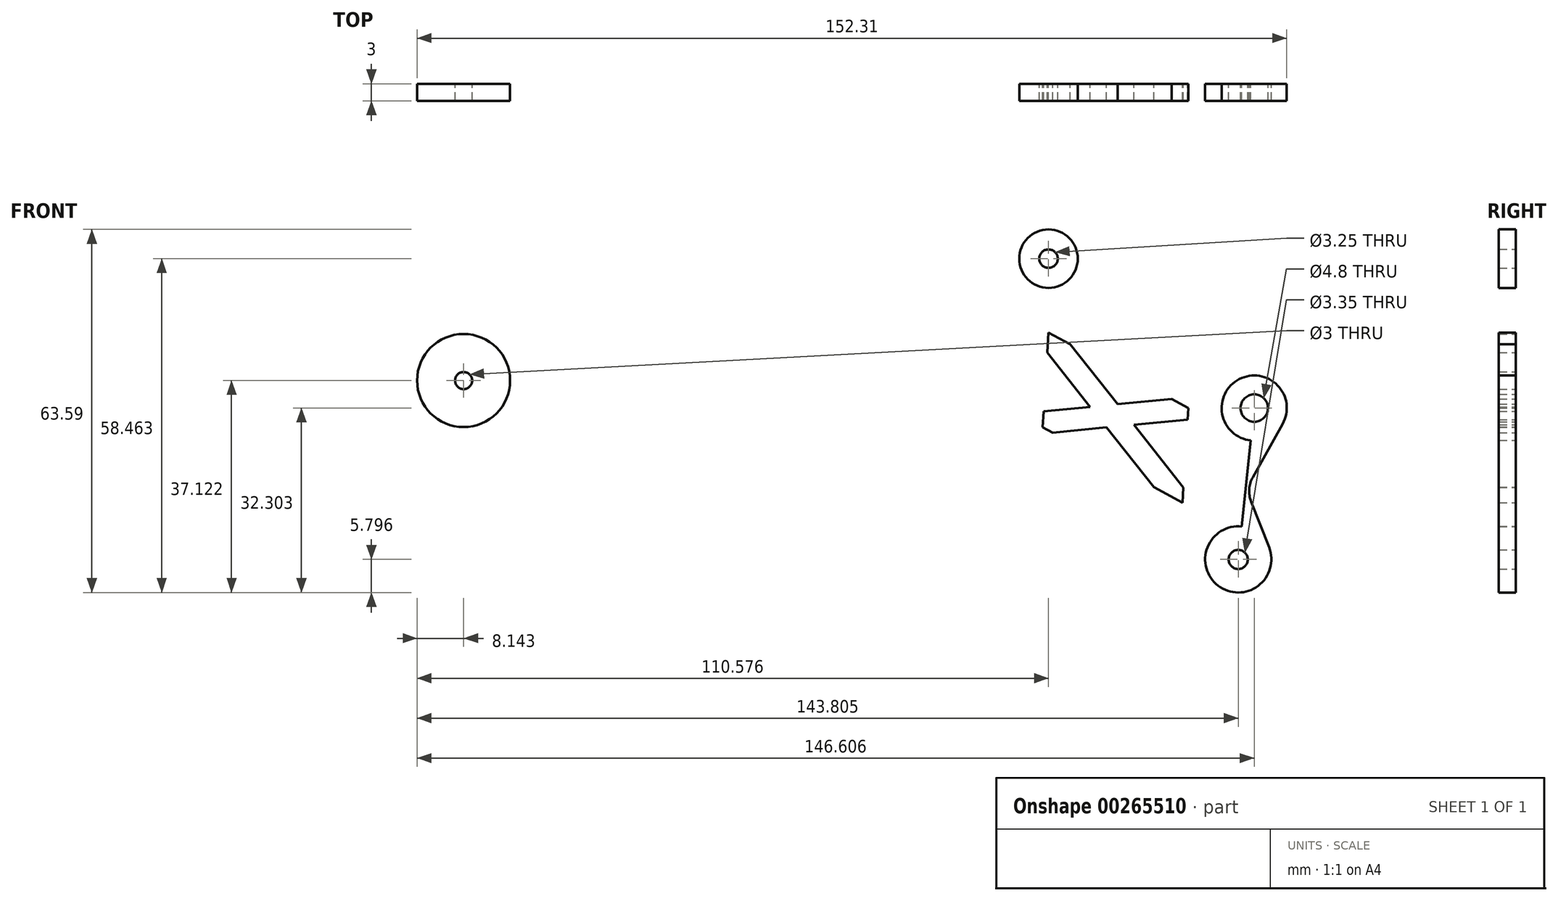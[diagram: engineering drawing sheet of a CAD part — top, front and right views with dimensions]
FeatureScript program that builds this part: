
annotation { "Feature Type Name" : "Feature", "Feature Type Description" : "" }
export const myFeature = defineFeature(function(context is Context, id is Id, definition is map)
    precondition{}
    {
        {
            var Q0;
            Q0=qCreatedBy(makeId("Front.planeOp"),FACE);
            var sketch = newSketch(context, id + "F0", { "sketchPlane" : qUnion([Q0])});
            skLineSegment(sketch, "E0", {"start": v(-62, 21.3) * mm, "end": v(-26.39, 21.3) * mm, "construction": true});
            skLineSegment(sketch, "E1", {"start": v(-44.19, 33.22) * mm, "end": v(-44.19, 9.36) * mm, "construction": true});
            skCircle(sketch, "E2", {"center": v(-44.19, 21.3) * mm, "radius": 8 * mm});
            skLineSegment(sketch, "E3", {"start": v(-44.19, 21.3) * mm, "end": v(-44.19, 31.84) * mm, "construction": true});
            skCircle(sketch, "E4", {"center": v(-44.19, 31.84) * mm, "radius": 1.35 * mm});
            skLineSegment(sketch, "E5.MirrorCS", {"start": v(-44.19, 21.3) * mm, "end": v(-44.19, 10.74) * mm, "construction": true});
            skCircle(sketch, "E6.MirrorC", {"center": v(-44.19, 10.74) * mm, "radius": 1.35 * mm});
            skCircle(sketch, "E7", {"center": v(-14.5, 21.05) * mm, "radius": 18.1 * mm});
            skLineSegment(sketch, "E8", {"start": v(-14.5, 21.05) * mm, "end": v(-8.7, 21.05) * mm, "construction": true});
            skCircle(sketch, "E9", {"center": v(-8.7, 21.05) * mm, "radius": 18.1 * mm});
            skLineSegment(sketch, "E10", {"start": v(-46.93, 21.05) * mm, "end": v(14.5, 21.05) * mm, "construction": true});
            skLineSegment(sketch, "E11", {"start": v(-27, 0) * mm, "end": v(27, 0) * mm});
            skLineSegment(sketch, "E12", {"start": v(-14.5, 2.95) * mm, "end": v(-8.7, 2.95) * mm});
            skLineSegment(sketch, "E13", {"start": v(27, 0) * mm, "end": v(27, 96) * mm, "construction": true});
            skLineSegment(sketch, "E14", {"start": v(-27, 0) * mm, "end": v(-27, 100) * mm, "construction": true});
            skLineSegment(sketch, "E15", {"start": v(-27, 100) * mm, "end": v(27, 96) * mm});
            skLineSegment(sketch, "E16", {"start": v(27, 96) * mm, "end": v(32.9, 95.56) * mm});
            skLineSegment(sketch, "E17", {"start": v(-56.51, 95.62) * mm, "end": v(-9.94, 92.16) * mm, "construction": true});
            skLineSegment(sketch, "E18.bottom", {"start": v(-7.95, 92) * mm, "end": v(29.75, 89.22) * mm});
            skLineSegment(sketch, "E18.top", {"start": v(-9.55, 70.37) * mm, "end": v(28.15, 67.58) * mm});
            skLineSegment(sketch, "E18.left", {"start": v(-10.09, 90.16) * mm, "end": v(-11.4, 72.5) * mm});
            skLineSegment(sketch, "E18.right", {"start": v(31.6, 87.07) * mm, "end": v(30.29, 69.42) * mm});
            skLineSegment(sketch, "E19", {"start": v(-10.74, 81.34) * mm, "end": v(-13.74, 81.56) * mm, "construction": true});
            skLineSegment(sketch, "E20", {"start": v(-10.74, 81.34) * mm, "end": v(-10.52, 84.33) * mm, "construction": true});
            skArc(sketch, "E21", {"start": v(-13.74, 81.56) * mm, "mid": v(-12.7, 83.6) * mm, "end": v(-10.52, 84.33) * mm});
            skArc(sketch, "E22", {"start": v(-13.74, 81.56) * mm, "mid": v(-13.02, 79.38) * mm, "end": v(-10.97, 78.34) * mm});
            skLineSegment(sketch, "E23", {"start": v(10.9, 90.61) * mm, "end": v(9.3, 68.97) * mm, "construction": true});
            skArc(sketch, "E24.MirrorCS", {"start": v(33.93, 78.03) * mm, "mid": v(32.9, 75.98) * mm, "end": v(30.72, 75.26) * mm});
            skArc(sketch, "E25.MirrorCS", {"start": v(33.93, 78.03) * mm, "mid": v(33.21, 80.2) * mm, "end": v(31.16, 81.24) * mm});
            skLineSegment(sketch, "E26", {"start": v(-10.74, 81.34) * mm, "end": v(-10.36, 86.47) * mm, "construction": true});
            skLineSegment(sketch, "E27", {"start": v(-10.36, 86.47) * mm, "end": v(-13.9, 86.73) * mm, "construction": true});
            skCircle(sketch, "E28", {"center": v(-13.9, 86.73) * mm, "radius": 1.55 * mm});
            skCircle(sketch, "E29.MirrorC", {"center": v(-14.66, 76.46) * mm, "radius": 1.55 * mm});
            skLineSegment(sketch, "E30.MirrorCS", {"start": v(-11.12, 76.2) * mm, "end": v(-14.66, 76.46) * mm, "construction": true});
            skLineSegment(sketch, "E31.MirrorCS", {"start": v(-10.74, 81.34) * mm, "end": v(-11.12, 76.2) * mm, "construction": true});
            skLineSegment(sketch, "E32.MirrorCS", {"start": v(30.56, 73.11) * mm, "end": v(34.1, 72.85) * mm, "construction": true});
            skCircle(sketch, "E33.MirrorC", {"center": v(34.1, 72.85) * mm, "radius": 1.55 * mm});
            skCircle(sketch, "E34.MirrorC", {"center": v(34.86, 83.12) * mm, "radius": 1.55 * mm});
            skLineSegment(sketch, "E35.MirrorCS", {"start": v(31.32, 83.38) * mm, "end": v(34.86, 83.12) * mm, "construction": true});
            skPoint(sketch, "E36.visualSharp", {"position": v(-9.94, 92.16) * mm});
            skArc(sketch, "E36.filletArc", {"start": v(-7.95, 92) * mm, "mid": v(-9.4, 91.53) * mm, "end": v(-10.09, 90.16) * mm});
            skPoint(sketch, "E37.visualSharp", {"position": v(-11.54, 70.52) * mm});
            skArc(sketch, "E37.filletArc", {"start": v(-11.4, 72.5) * mm, "mid": v(-10.92, 71.06) * mm, "end": v(-9.55, 70.37) * mm});
            skPoint(sketch, "E38.visualSharp", {"position": v(31.74, 89.07) * mm});
            skArc(sketch, "E38.filletArc", {"start": v(31.6, 87.07) * mm, "mid": v(31.12, 88.53) * mm, "end": v(29.75, 89.22) * mm});
            skPoint(sketch, "E39.visualSharp", {"position": v(30.14, 67.43) * mm});
            skArc(sketch, "E39.filletArc", {"start": v(28.15, 67.58) * mm, "mid": v(29.6, 68.06) * mm, "end": v(30.29, 69.42) * mm});
            skLineSegment(sketch, "E40.bottom", {"start": v(17.59, 51.31) * mm, "end": v(55.28, 48.52) * mm});
            skLineSegment(sketch, "E40.top", {"start": v(15.98, 29.67) * mm, "end": v(53.68, 26.88) * mm});
            skLineSegment(sketch, "E40.left", {"start": v(15.44, 49.46) * mm, "end": v(14.14, 31.81) * mm});
            skLineSegment(sketch, "E40.right", {"start": v(57.13, 46.38) * mm, "end": v(55.82, 28.72) * mm});
            skLineSegment(sketch, "E41", {"start": v(14.79, 40.64) * mm, "end": v(11.8, 40.86) * mm, "construction": true});
            skLineSegment(sketch, "E42", {"start": v(14.79, 40.64) * mm, "end": v(15.01, 43.63) * mm, "construction": true});
            skArc(sketch, "E43", {"start": v(11.8, 40.86) * mm, "mid": v(12.83, 42.91) * mm, "end": v(15.01, 43.63) * mm});
            skArc(sketch, "E44", {"start": v(11.8, 40.86) * mm, "mid": v(12.52, 38.68) * mm, "end": v(14.57, 37.65) * mm});
            skLineSegment(sketch, "E45", {"start": v(36.43, 49.91) * mm, "end": v(34.83, 28.27) * mm, "construction": true});
            skArc(sketch, "E46.MirrorCS", {"start": v(59.47, 37.33) * mm, "mid": v(58.43, 35.28) * mm, "end": v(56.25, 34.56) * mm});
            skArc(sketch, "E47.MirrorCS", {"start": v(59.47, 37.33) * mm, "mid": v(58.75, 39.5) * mm, "end": v(56.7, 40.54) * mm});
            skLineSegment(sketch, "E48", {"start": v(14.79, 40.64) * mm, "end": v(15.17, 45.77) * mm, "construction": true});
            skLineSegment(sketch, "E49", {"start": v(15.17, 45.77) * mm, "end": v(11.63, 46.04) * mm, "construction": true});
            skCircle(sketch, "E50", {"center": v(11.63, 46.04) * mm, "radius": 1.55 * mm});
            skCircle(sketch, "E51.MirrorC", {"center": v(10.87, 35.76) * mm, "radius": 1.55 * mm});
            skLineSegment(sketch, "E52.MirrorCS", {"start": v(14.4, 35.5) * mm, "end": v(10.87, 35.76) * mm, "construction": true});
            skLineSegment(sketch, "E53.MirrorCS", {"start": v(14.79, 40.64) * mm, "end": v(14.4, 35.5) * mm, "construction": true});
            skLineSegment(sketch, "E54.MirrorCS", {"start": v(56.1, 32.41) * mm, "end": v(59.64, 32.15) * mm, "construction": true});
            skCircle(sketch, "E55.MirrorC", {"center": v(59.64, 32.15) * mm, "radius": 1.55 * mm});
            skCircle(sketch, "E56.MirrorC", {"center": v(60.4, 42.42) * mm, "radius": 1.55 * mm});
            skLineSegment(sketch, "E57.MirrorCS", {"start": v(56.86, 42.69) * mm, "end": v(60.4, 42.42) * mm, "construction": true});
            skPoint(sketch, "E58.visualSharp", {"position": v(15.6, 51.46) * mm});
            skArc(sketch, "E58.filletArc", {"start": v(17.59, 51.31) * mm, "mid": v(16.13, 50.83) * mm, "end": v(15.44, 49.46) * mm});
            skPoint(sketch, "E59.visualSharp", {"position": v(13.99, 29.82) * mm});
            skArc(sketch, "E59.filletArc", {"start": v(14.14, 31.81) * mm, "mid": v(14.62, 30.36) * mm, "end": v(15.98, 29.67) * mm});
            skPoint(sketch, "E60.visualSharp", {"position": v(57.28, 48.37) * mm});
            skArc(sketch, "E60.filletArc", {"start": v(57.13, 46.38) * mm, "mid": v(56.65, 47.83) * mm, "end": v(55.28, 48.52) * mm});
            skPoint(sketch, "E61.visualSharp", {"position": v(55.67, 26.73) * mm});
            skArc(sketch, "E61.filletArc", {"start": v(53.68, 26.88) * mm, "mid": v(55.13, 27.36) * mm, "end": v(55.82, 28.72) * mm});
            skLineSegment(sketch, "E62", {"start": v(30.14, 67.43) * mm, "end": v(28.89, 50.47) * mm, "construction": true});
            skLineSegment(sketch, "E63", {"start": v(28.89, 50.47) * mm, "end": v(15.6, 51.46) * mm, "construction": true});
            skLineSegment(sketch, "E64", {"start": v(55.67, 26.73) * mm, "end": v(53.66, -0.52) * mm, "construction": true});
            skLineSegment(sketch, "E65", {"start": v(53.66, -0.52) * mm, "end": v(46.68, 0) * mm, "construction": true});
            skLineSegment(sketch, "E66", {"start": v(27, 0) * mm, "end": v(46.68, 0) * mm});
            skLineSegment(sketch, "E67", {"start": v(60.4, 42.42) * mm, "end": v(88.4, 62) * mm, "construction": true});
            skLineSegment(sketch, "E68", {"start": v(34.1, 72.85) * mm, "end": v(88.4, 62) * mm, "construction": true});
            skCircle(sketch, "E69", {"center": v(88.4, 62) * mm, "radius": 1.68 * mm});
            skLineSegment(sketch, "E70", {"start": v(60.4, 42.42) * mm, "end": v(69.22, 57.07) * mm, "construction": true});
            skLineSegment(sketch, "E71", {"start": v(34.1, 72.85) * mm, "end": v(69.22, 57.07) * mm, "construction": true});
            skCircle(sketch, "E72", {"center": v(69.22, 57.07) * mm, "radius": 2 * mm});
            skLineSegment(sketch, "E73", {"start": v(60.4, 42.42) * mm, "end": v(77.84, 65.53) * mm, "construction": true});
            skLineSegment(sketch, "E74", {"start": v(34.1, 72.85) * mm, "end": v(77.84, 65.53) * mm, "construction": true});
            skCircle(sketch, "E75", {"center": v(77.84, 65.53) * mm, "radius": 1.25 * mm});
            skLineSegment(sketch, "E76", {"start": v(59.64, 32.15) * mm, "end": v(91.2, 88.51) * mm, "construction": true});
            skLineSegment(sketch, "E77", {"start": v(34.86, 83.12) * mm, "end": v(91.2, 88.51) * mm, "construction": true});
            skCircle(sketch, "E78", {"center": v(91.2, 88.51) * mm, "radius": 2.4 * mm});
            skLineSegment(sketch, "E79", {"start": v(59.64, 32.15) * mm, "end": v(34.5, 58.07) * mm, "construction": true});
            skLineSegment(sketch, "E80", {"start": v(10.87, 35.76) * mm, "end": v(34.5, 58.07) * mm, "construction": true});
            skCircle(sketch, "E81", {"center": v(34.5, 58.07) * mm, "radius": 2 * mm});
            skLineSegment(sketch, "E82", {"start": v(34.86, 83.12) * mm, "end": v(55.18, 114.67) * mm, "construction": true});
            skLineSegment(sketch, "E83", {"start": v(91.2, 88.51) * mm, "end": v(55.18, 114.67) * mm, "construction": true});
            skCircle(sketch, "E84", {"center": v(55.18, 114.67) * mm, "radius": 1.63 * mm});
            skLineSegment(sketch, "E85", {"start": v(59.64, 32.15) * mm, "end": v(13.17, 19.73) * mm, "construction": true});
            skLineSegment(sketch, "E86", {"start": v(10.87, 35.76) * mm, "end": v(13.17, 19.73) * mm, "construction": true});
            skCircle(sketch, "E87", {"center": v(13.17, 19.73) * mm, "radius": 1.5 * mm});
            skLineSegment(sketch, "E88", {"start": v(59.64, 32.15) * mm, "end": v(15.67, 5.14) * mm, "construction": true});
            skLineSegment(sketch, "E89", {"start": v(15.67, 5.14) * mm, "end": v(10.87, 35.76) * mm, "construction": true});
            skCircle(sketch, "E90", {"center": v(15.67, 5.14) * mm, "radius": 1.5 * mm});
            skLineSegment(sketch, "E91", {"start": v(59.64, 32.15) * mm, "end": v(4.5, 5.12) * mm, "construction": true});
            skLineSegment(sketch, "E92", {"start": v(4.5, 5.12) * mm, "end": v(10.87, 35.76) * mm, "construction": true});
            skCircle(sketch, "E93", {"center": v(4.5, 5.12) * mm, "radius": 1.5 * mm});
            skLineSegment(sketch, "E94", {"start": v(-14.66, 76.46) * mm, "end": v(5.35, 55.37) * mm, "construction": true});
            skLineSegment(sketch, "E95", {"start": v(11.63, 46.04) * mm, "end": v(5.35, 55.37) * mm, "construction": true});
            skLineSegment(sketch, "E96", {"start": v(11.63, 46.04) * mm, "end": v(-9.77, 54.86) * mm, "construction": true});
            skLineSegment(sketch, "E97", {"start": v(-9.77, 54.86) * mm, "end": v(-14.66, 76.46) * mm, "construction": true});
            skLineSegment(sketch, "E98", {"start": v(11.63, 46.04) * mm, "end": v(-18.73, 56.32) * mm, "construction": true});
            skLineSegment(sketch, "E99", {"start": v(-18.73, 56.32) * mm, "end": v(-14.66, 76.46) * mm, "construction": true});
            skCircle(sketch, "E100", {"center": v(5.35, 55.37) * mm, "radius": 1.5 * mm});
            skCircle(sketch, "E101", {"center": v(-9.77, 54.86) * mm, "radius": 1.6 * mm});
            skCircle(sketch, "E102", {"center": v(-18.73, 56.32) * mm, "radius": 1.6 * mm});
            skLineSegment(sketch, "E103", {"start": v(11.63, 46.04) * mm, "end": v(-22.31, 42.26) * mm, "construction": true});
            skLineSegment(sketch, "E104", {"start": v(-22.31, 42.26) * mm, "end": v(-14.66, 76.46) * mm, "construction": true});
            skCircle(sketch, "E105", {"center": v(-22.31, 42.26) * mm, "radius": 1.5 * mm});
            skLineSegment(sketch, "E106", {"start": v(11.63, 46.04) * mm, "end": v(-34.4, 4.89) * mm, "construction": true});
            skLineSegment(sketch, "E107", {"start": v(-34.4, 4.89) * mm, "end": v(-14.66, 76.46) * mm, "construction": true});
            skCircle(sketch, "E108", {"center": v(-34.4, 4.89) * mm, "radius": 1.5 * mm});
            skLineSegment(sketch, "E109", {"start": v(-14.66, 76.46) * mm, "end": v(-21.38, 70.03) * mm, "construction": true});
            skLineSegment(sketch, "E110", {"start": v(-21.38, 70.03) * mm, "end": v(-13.9, 86.73) * mm, "construction": true});
            skCircle(sketch, "E111", {"center": v(-21.38, 70.03) * mm, "radius": 1.5 * mm});
            skLineSegment(sketch, "E112", {"start": v(-14.66, 76.46) * mm, "end": v(-22.42, 74.5) * mm, "construction": true});
            skLineSegment(sketch, "E113", {"start": v(-22.42, 74.5) * mm, "end": v(-13.9, 86.73) * mm, "construction": true});
            skCircle(sketch, "E114", {"center": v(-22.42, 74.5) * mm, "radius": 1.5 * mm});
            skLineSegment(sketch, "E115", {"start": v(-14.66, 76.46) * mm, "end": v(-23.4, 78.61) * mm, "construction": true});
            skLineSegment(sketch, "E116", {"start": v(-23.4, 78.61) * mm, "end": v(-13.9, 86.73) * mm, "construction": true});
            skCircle(sketch, "E117", {"center": v(-23.4, 78.61) * mm, "radius": 1.5 * mm});
            skLineSegment(sketch, "E118", {"start": v(-14.66, 76.46) * mm, "end": v(-20.12, 82.72) * mm, "construction": true});
            skLineSegment(sketch, "E119", {"start": v(-20.12, 82.72) * mm, "end": v(-13.9, 86.73) * mm, "construction": true});
            skCircle(sketch, "E120", {"center": v(-20.12, 82.72) * mm, "radius": 1.5 * mm});
            skLineSegment(sketch, "E121", {"start": v(-14.66, 76.46) * mm, "end": v(-24.8, 88.18) * mm, "construction": true});
            skLineSegment(sketch, "E122", {"start": v(-24.8, 88.18) * mm, "end": v(-13.9, 86.73) * mm, "construction": true});
            skCircle(sketch, "E123", {"center": v(-24.8, 88.18) * mm, "radius": 1.5 * mm});
            skLineSegment(sketch, "E124", {"start": v(-14.66, 76.46) * mm, "end": v(-47.26, 93.33) * mm, "construction": true});
            skLineSegment(sketch, "E125", {"start": v(-47.26, 93.33) * mm, "end": v(-13.9, 86.73) * mm, "construction": true});
            skCircle(sketch, "E126", {"center": v(-47.26, 93.33) * mm, "radius": 1.5 * mm});
            skLineSegment(sketch, "E127", {"start": v(-14.66, 76.46) * mm, "end": v(-36, 89.67) * mm, "construction": true});
            skLineSegment(sketch, "E128", {"start": v(-36, 89.67) * mm, "end": v(-13.9, 86.73) * mm, "construction": true});
            skCircle(sketch, "E129", {"center": v(-36, 89.67) * mm, "radius": 2.5 * mm});
            skLineSegment(sketch, "E130", {"start": v(13.17, 19.73) * mm, "end": v(-8.7, 21.05) * mm, "construction": true});
            skLineSegment(sketch, "E131", {"start": v(-22.31, 42.26) * mm, "end": v(-14.5, 21.05) * mm, "construction": true});
            skLineSegment(sketch, "E132", {"start": v(-22.31, 42.26) * mm, "end": v(-44.19, 21.3) * mm, "construction": true});
            skLineSegment(sketch, "E133", {"start": v(-34.4, 4.89) * mm, "end": v(-44.19, 21.3) * mm, "construction": true});
            skCircle(sketch, "E134", {"center": v(57.5, 17.56) * mm, "radius": 3.75 * mm});
            skCircle(sketch, "E135", {"center": v(53.23, 12.26) * mm, "radius": 3.75 * mm});
            skLineSegment(sketch, "E136", {"start": v(53.23, 12.26) * mm, "end": v(57.5, 17.56) * mm, "construction": true});
            skLineSegment(sketch, "E137", {"start": v(50.3, 14.61) * mm, "end": v(54.57, 19.91) * mm});
            skLineSegment(sketch, "E138", {"start": v(56.15, 9.91) * mm, "end": v(60.41, 15.2) * mm});
            skLineSegment(sketch, "E139", {"start": v(59.64, 32.15) * mm, "end": v(57.5, 17.56) * mm, "construction": true});
            skLineSegment(sketch, "E140", {"start": v(10.87, 35.76) * mm, "end": v(57.5, 17.56) * mm, "construction": true});
            skLineSegment(sketch, "E141", {"start": v(13.17, 19.73) * mm, "end": v(53.23, 12.26) * mm, "construction": true});
            skLineSegment(sketch, "E142", {"start": v(59.64, 32.15) * mm, "end": v(44.47, 5.11) * mm, "construction": true});
            skLineSegment(sketch, "E143", {"start": v(15.67, 5.14) * mm, "end": v(44.47, 5.11) * mm, "construction": true});
            skCircle(sketch, "E144", {"center": v(44.47, 5.11) * mm, "radius": 1.5 * mm});
            skLineSegment(sketch, "E145", {"start": v(93.6, 88.51) * mm, "end": v(96.9, 88.51) * mm, "construction": true});
            skLineSegment(sketch, "E146", {"start": v(90.08, 62) * mm, "end": v(94.2, 62) * mm, "construction": true});
            skLineSegment(sketch, "E147", {"start": v(55.18, 116.3) * mm, "end": v(55.18, 119.8) * mm, "construction": true});
            skCircle(sketch, "E148", {"center": v(55.18, 114.67) * mm, "radius": 5.12 * mm});
            skCircle(sketch, "E149", {"center": v(91.2, 88.51) * mm, "radius": 5.7 * mm});
            skLineSegment(sketch, "E150", {"start": v(58.13, 118.86) * mm, "end": v(94.5, 93.17) * mm});
            skCircle(sketch, "E151", {"center": v(88.4, 62) * mm, "radius": 5.8 * mm});
            skLineSegment(sketch, "E152", {"start": v(91.2, 88.51) * mm, "end": v(88.4, 62) * mm});
            skLineSegment(sketch, "E153", {"start": v(96.18, 85.73) * mm, "end": v(90.96, 76.41) * mm});
            skPoint(sketch, "E153.endSnap0", {"position": v(89.8, 75.26) * mm});
            skLineSegment(sketch, "E154", {"start": v(90.67, 72.15) * mm, "end": v(93.8, 64.11) * mm});
            skPoint(sketch, "E155.visualSharp", {"position": v(89.8, 74.35) * mm});
            skArc(sketch, "E155.filletArc", {"start": v(90.96, 76.41) * mm, "mid": v(90.33, 74.31) * mm, "end": v(90.67, 72.15) * mm});
            skLineSegment(sketch, "E156", {"start": v(61.95, 42.42) * mm, "end": v(74.45, 42.42) * mm, "construction": true});
            skLineSegment(sketch, "E157", {"start": v(61.19, 32.15) * mm, "end": v(68.49, 32.15) * mm, "construction": true});
            skLineSegment(sketch, "E158", {"start": v(61.24, 17.56) * mm, "end": v(65.04, 17.56) * mm, "construction": true});
            skLineSegment(sketch, "E159", {"start": v(53.23, 8.51) * mm, "end": v(53.23, 0.01) * mm, "construction": true});
            skFitSpline(sketch, "E160", {"points": [v(91.65, 57.2) * mm, v(74.45, 42.42) * mm, v(68.49, 32.15) * mm, v(65.04, 17.56) * mm, v(53.23, 0.01) * mm, v(46.68, 0) * mm], "startDerivative": vector(-74.62, -50.51) * mm, "endDerivative": vector(-25.22, -6.26) * mm});
            skLineSegment(sketch, "E161", {"start": v(46.68, 0) * mm, "end": v(46.68, 0) * mm});
            skLineSegment(sketch, "E162", {"start": v(-44.19, 9.4) * mm, "end": v(-44.19, 4.4) * mm, "construction": true});
            skLineSegment(sketch, "E163", {"start": v(-52.19, 21.3) * mm, "end": v(-54.19, 21.3) * mm, "construction": true});
            skFitSpline(sketch, "E164", {"points": [v(-27, 0) * mm, v(-44.19, 4.4) * mm, v(-54.19, 21.3) * mm], "startDerivative": vector(-54.76, 2.17) * mm, "endDerivative": vector(-15.42, 42.63) * mm});
            skLineSegment(sketch, "E165", {"start": v(-20.33, 56.32) * mm, "end": v(-24.13, 56.32) * mm, "construction": true});
            skLineSegment(sketch, "E166", {"start": v(-44.19, 33.2) * mm, "end": v(-44.19, 37.2) * mm, "construction": true});
            skLineSegment(sketch, "E167", {"start": v(-22.88, 70.03) * mm, "end": v(-27.23, 70.03) * mm, "construction": true});
            skLineSegment(sketch, "E168", {"start": v(-23.92, 74.5) * mm, "end": v(-28.57, 74.5) * mm, "construction": true});
            skLineSegment(sketch, "E169", {"start": v(-45.54, 31.84) * mm, "end": v(-52.94, 31.84) * mm, "construction": true});
            skLineSegment(sketch, "E170", {"start": v(-54.19, 21.3) * mm, "end": v(-52.94, 31.84) * mm});
            skLineSegment(sketch, "E171", {"start": v(-24.9, 78.61) * mm, "end": v(-29.5, 78.61) * mm, "construction": true});
            skFitSpline(sketch, "E172", {"points": [v(-29.5, 78.61) * mm, v(-28.57, 74.5) * mm, v(-27.23, 70.03) * mm, v(-24.13, 56.32) * mm, v(-44.19, 37.2) * mm, v(-44.19, 37.2) * mm, v(-52.94, 31.84) * mm], "startDerivative": vector(22.4, -98.57) * mm, "endDerivative": vector(-34.9, -32.52) * mm});
            skLineSegment(sketch, "E173", {"start": v(-29.5, 78.61) * mm, "end": v(-27.23, 70.03) * mm});
            skCircle(sketch, "E174", {"center": v(-47.26, 93.33) * mm, "radius": 8.15 * mm});
            skLineSegment(sketch, "E175", {"start": v(-27, 100) * mm, "end": v(-46.66, 101.46) * mm});
            skLineSegment(sketch, "E176", {"start": v(-29.5, 78.61) * mm, "end": v(-49.9, 85.63) * mm});
            skLineSegment(sketch, "E177", {"start": v(-47.26, 94.93) * mm, "end": v(-46.66, 101.46) * mm, "construction": true});
            skLineSegment(sketch, "E178", {"start": v(34.1, 72.85) * mm, "end": v(35.77, 95.35) * mm, "construction": true});
            skLineSegment(sketch, "E179", {"start": v(37.4, 97.73) * mm, "end": v(50.94, 117.56) * mm});
            skPoint(sketch, "E180.visualSharp", {"position": v(35.77, 95.35) * mm});
            skArc(sketch, "E180.filletArc", {"start": v(32.9, 95.56) * mm, "mid": v(35.43, 96.04) * mm, "end": v(37.4, 97.73) * mm});
            skLineSegment(sketch, "E181", {"start": v(53.23, 0.01) * mm, "end": v(46.68, 0) * mm});
            skLineSegment(sketch, "E182", {"start": v(55.18, 113.05) * mm, "end": v(55.18, 101.75) * mm, "construction": true});
            skLineSegment(sketch, "E183", {"start": v(88.8, 88.51) * mm, "end": v(79.66, 88.51) * mm, "construction": true});
            skLineSegment(sketch, "E184", {"start": v(55.18, 101.75) * mm, "end": v(79.66, 88.51) * mm});
            skLineSegment(sketch, "E185", {"start": v(79.66, 88.51) * mm, "end": v(78.62, 71.94) * mm});
            skLineSegment(sketch, "E186", {"start": v(55.18, 101.75) * mm, "end": v(54.15, 85.17) * mm});
            skLineSegment(sketch, "E187", {"start": v(54.15, 85.17) * mm, "end": v(78.62, 71.94) * mm});
            skLineSegment(sketch, "E188", {"start": v(54.96, 98.23) * mm, "end": v(73.6, 74.65) * mm});
            skLineSegment(sketch, "E189", {"start": v(58.96, 99.7) * mm, "end": v(78.8, 74.63) * mm});
            skLineSegment(sketch, "E190", {"start": v(54.32, 87.95) * mm, "end": v(76.73, 90.1) * mm});
            skLineSegment(sketch, "E191", {"start": v(55.9, 84.22) * mm, "end": v(79.53, 86.48) * mm});
            skPoint(sketch, "E192", {"position": v(62.47, 88.73) * mm});
            skPoint(sketch, "E193", {"position": v(67.28, 89.19) * mm});
            skPoint(sketch, "E194", {"position": v(70.13, 85.58) * mm});
            skPoint(sketch, "E195", {"position": v(65.33, 85.12) * mm});
            skLineSegment(sketch, "E196", {"start": v(77.84, 65.53) * mm, "end": v(44.65, 81.4) * mm, "construction": true});
            skLineSegment(sketch, "E197", {"start": v(91.2, 88.51) * mm, "end": v(44.65, 81.4) * mm, "construction": true});
            skCircle(sketch, "E198", {"center": v(44.65, 81.4) * mm, "radius": 2 * mm});
            skLineSegment(sketch, "E199", {"start": v(69.22, 57.07) * mm, "end": v(61.62, 64.6) * mm, "construction": true});
            skLineSegment(sketch, "E200", {"start": v(44.65, 81.4) * mm, "end": v(61.62, 64.6) * mm, "construction": true});
            skCircle(sketch, "E201", {"center": v(61.62, 64.6) * mm, "radius": 1.4 * mm});
            skLineSegment(sketch, "E202", {"start": v(-14.5, 39.15) * mm, "end": v(-8.7, 39.15) * mm});
            skSolve(sketch);
        }
        {
            var Q0;
            Q0=makeQuery(id+"F0.imprint","IMPRINT",FACE,{"disambiguationData":[TD([[makeQuery(id+"F0.imprint","IMPRINT",EDGE,{"derivedFrom":sQuery(id+"F0.wireOp",EDGE,"E2")}),-1.0]])]});
            var Q1;
            Q1=makeQuery(id+"F0.imprint","IMPRINT",FACE,{"disambiguationData":[TD([[makeQuery(id+"F0.imprint","IMPRINT",EDGE,{"derivedFrom":sQuery(id+"F0.wireOp",EDGE,"E126")}),-1.0]])]});
            var Q2;
            Q2=makeQuery(id+"F0.imprint","IMPRINT",FACE,{"disambiguationData":[TD([[makeQuery(id+"F0.imprint","IMPRINT",EDGE,{"derivedFrom":sQuery(id+"F0.wireOp",EDGE,"E84")}),-1.0]])]});
            var Q3;
            Q3=makeQuery(id+"F0.imprint","IMPRINT",FACE,{"disambiguationData":[TD([[makeQuery(id+"F0.imprint","IMPRINT",EDGE,{"derivedFrom":sQuery(id+"F0.wireOp",EDGE,"E78")}),-1.0]])]});
            var Q4;
            Q4=makeQuery(id+"F0.imprint","IMPRINT",FACE,{"disambiguationData":[TD([[makeQuery(id+"F0.imprint","IMPRINT",EDGE,{"derivedFrom":sQuery(id+"F0.wireOp",EDGE,"E69")}),-1.0]])]});
            var Q5;
            {var subQ0=sQuery(id+"F0.wireOp",EDGE,"E153");Q5=makeQuery(id+"F0.imprint","IMPRINT",FACE,{"disambiguationData":[TD([[makeQuery(id+"F0.imprint","IMPRINT",EDGE,{"derivedFrom":subQ0}),-1.0]])]});}
            var Q6;
            {var subQ1=sQuery(id+"F0.wireOp",EDGE,"E186");var subQ5=sQuery(id+"F0.wireOp",EDGE,"E184");var subQ6=makeQuery(id+"F0.imprint","INTERSECT",VERTEX,{"derivedFrom":[subQ5,subQ1]});Q6=makeQuery(id+"F0.imprint","IMPRINT",FACE,{"disambiguationData":[TD([[makeQuery(id+"F0.imprint","IMPRINT",EDGE,{"disambiguationData":[TD([[subQ6,-1.0]])],"derivedFrom":subQ5}),-1.0]])]});}
            var Q7;
            {var subQ0=sQuery(id+"F0.wireOp",EDGE,"E190");var subQ1=sQuery(id+"F0.wireOp",EDGE,"E188");var subQ2=makeQuery(id+"F0.imprint","INTERSECT",VERTEX,{"derivedFrom":[subQ1,subQ0]});Q7=makeQuery(id+"F0.imprint","IMPRINT",FACE,{"disambiguationData":[TD([[makeQuery(id+"F0.imprint","IMPRINT",EDGE,{"disambiguationData":[TD([[subQ2,-1.0]])],"derivedFrom":subQ1}),1.0]])]});}
            var Q8;
            {var subQ0=sQuery(id+"F0.wireOp",EDGE,"E187");var subQ1=sQuery(id+"F0.wireOp",EDGE,"E186");var subQ2=makeQuery(id+"F0.imprint","INTERSECT",VERTEX,{"derivedFrom":[subQ1,subQ0]});Q8=makeQuery(id+"F0.imprint","IMPRINT",FACE,{"disambiguationData":[TD([[makeQuery(id+"F0.imprint","IMPRINT",EDGE,{"disambiguationData":[TD([[subQ2,1.0]])],"derivedFrom":subQ1}),1.0]])]});}
            var Q9;
            {var subQ1=sQuery(id+"F0.wireOp",EDGE,"E185");var subQ6=sQuery(id+"F0.wireOp",EDGE,"E187");var subQ9=makeQuery(id+"F0.imprint","INTERSECT",VERTEX,{"derivedFrom":[subQ1,subQ6]});Q9=makeQuery(id+"F0.imprint","IMPRINT",FACE,{"disambiguationData":[TD([[makeQuery(id+"F0.imprint","IMPRINT",EDGE,{"disambiguationData":[TD([[subQ9,1.0]])],"derivedFrom":subQ1}),-1.0]])]});}
            var Q10;
            {var subQ1=sQuery(id+"F0.wireOp",EDGE,"E184");var subQ7=sQuery(id+"F0.wireOp",EDGE,"E185");var subQ8=makeQuery(id+"F0.imprint","INTERSECT",VERTEX,{"derivedFrom":[subQ1,subQ7]});Q10=makeQuery(id+"F0.imprint","IMPRINT",FACE,{"disambiguationData":[TD([[makeQuery(id+"F0.imprint","IMPRINT",EDGE,{"disambiguationData":[TD([[subQ8,1.0]])],"derivedFrom":subQ1}),-1.0]])]});}
            extrude(context, id + "F1", {"entities" : qUnion([Q0, Q1, Q2, Q3, Q4, Q5, Q6, Q7, Q8, Q9, Q10]), "depth" : 3 * mm, "offsetDistance" : 25 * mm});
        }
    });
